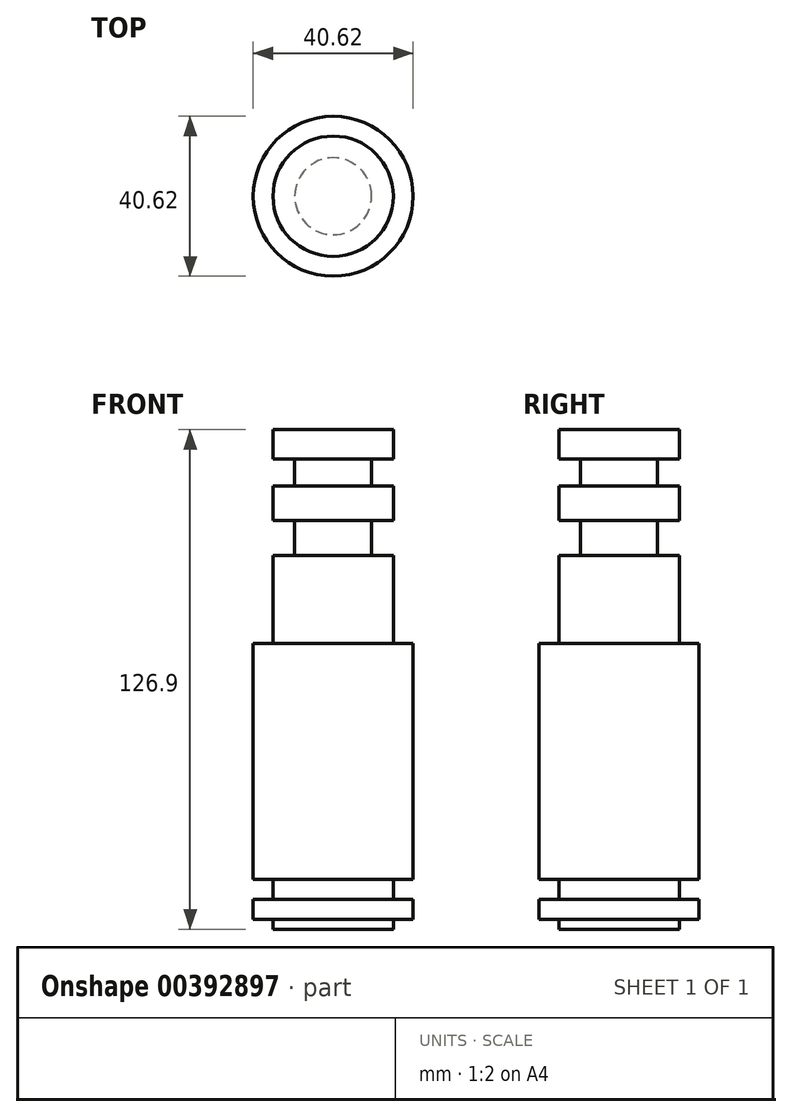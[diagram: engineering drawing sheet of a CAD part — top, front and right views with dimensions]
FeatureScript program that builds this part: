
annotation { "Feature Type Name" : "Feature", "Feature Type Description" : "" }
export const myFeature = defineFeature(function(context is Context, id is Id, definition is map)
    precondition{}
    {
        {
            var Q0;
            Q0=qCreatedBy(makeId("Front.planeOp"),FACE);
            var sketch = newSketch(context, id + "F0", { "sketchPlane" : qUnion([Q0])});
            skLineSegment(sketch, "E0", {"start": v(0, 54.36) * mm, "end": v(0, -72.54) * mm});
            skLineSegment(sketch, "E1", {"start": v(0, 54.36) * mm, "end": v(15.3, 54.36) * mm});
            skLineSegment(sketch, "E2", {"start": v(15.3, 54.36) * mm, "end": v(15.3, 46.88) * mm});
            skLineSegment(sketch, "E3", {"start": v(15.3, 46.88) * mm, "end": v(9.77, 46.88) * mm});
            skLineSegment(sketch, "E4", {"start": v(9.77, 46.88) * mm, "end": v(9.77, 40) * mm});
            skLineSegment(sketch, "E5", {"start": v(9.77, 40) * mm, "end": v(15.3, 40) * mm});
            skLineSegment(sketch, "E6", {"start": v(15.3, 40) * mm, "end": v(15.3, 31.28) * mm});
            skLineSegment(sketch, "E7", {"start": v(15.3, 31.28) * mm, "end": v(9.77, 31.28) * mm});
            skLineSegment(sketch, "E8", {"start": v(9.77, 31.28) * mm, "end": v(9.77, 22.43) * mm});
            skLineSegment(sketch, "E9", {"start": v(9.77, 22.43) * mm, "end": v(15.3, 22.43) * mm});
            skLineSegment(sketch, "E10", {"start": v(15.3, 22.43) * mm, "end": v(15.3, 0) * mm});
            skLineSegment(sketch, "E11", {"start": v(15.3, 0) * mm, "end": v(20.3, 0) * mm});
            skLineSegment(sketch, "E12", {"start": v(20.3, 0) * mm, "end": v(20.3, -59.84) * mm});
            skLineSegment(sketch, "E13", {"start": v(20.3, -59.84) * mm, "end": v(15.3, -59.84) * mm});
            skLineSegment(sketch, "E14", {"start": v(15.3, -59.84) * mm, "end": v(15.3, -64.92) * mm});
            skLineSegment(sketch, "E15", {"start": v(15.3, -64.92) * mm, "end": v(20.3, -64.92) * mm});
            skLineSegment(sketch, "E16", {"start": v(20.3, -64.92) * mm, "end": v(20.3, -70) * mm});
            skLineSegment(sketch, "E17", {"start": v(20.3, -70) * mm, "end": v(15.3, -70) * mm});
            skLineSegment(sketch, "E18", {"start": v(15.3, -70) * mm, "end": v(15.3, -72.54) * mm});
            skLineSegment(sketch, "E19", {"start": v(15.3, -72.54) * mm, "end": v(0, -72.54) * mm});
            skSolve(sketch);
        }
        {
            var Q0;
            Q0=makeQuery(id+"F0.imprint","IMPRINT",FACE,{"disambiguationData":[TD([[makeQuery(id+"F0.imprint","IMPRINT",EDGE,{"derivedFrom":sQuery(id+"F0.wireOp",EDGE,"E0")}),1.0]])]});
            var Q1;
            Q1=sQuery(id+"F0.wireOp",EDGE,"E0");
            revolve(context, id + "F1", {"entities" : qUnion([Q0]), "axis" : qUnion([Q1]), "revolveType" : RevolveType.FULL});
        }
    });
